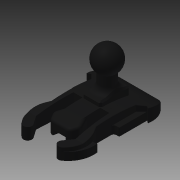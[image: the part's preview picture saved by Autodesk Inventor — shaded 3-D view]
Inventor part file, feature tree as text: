
AUTODESK INVENTOR PART (.ipt)
format: ipt  version: 2014 (Build 180170000, 170)  size: 611,840 bytes
history: native  units: in
note: dims shown in document units (in); Inventor stores cm internally (conversion verified against a paired STEP export)
features: sketch x4, other x3, extrude x3, chamfer x2, plane x1, revolve x1, fillet x1, imported_body x1
ambient origin geometry x8: Origin, YZ Plane, XZ Plane, XY Plane, X Axis, Y Axis, Z Axis, Center Point
bodies: Body1 (feature_tree)
feature tree (16):
  other  "Cut-Extrude3"
  other  "Quck Release - Mount - Standard (1)1"
  extrude  "Extrusion1"  [1 undecoded]
  plane  "Work Plane1"
  extrude  "Extrusion2"  Depth=0.3in
  extrude  "Extrusion3"  Depth=0.5in
  other  "Work Axis1"
  revolve  "Revolution1"  [1 undecoded]
  fillet  "Fillet1"  Radius=0.03in
  chamfer  "Chamfer1"  Distance=0.03in Angle=45.0deg
  chamfer  "Chamfer2"  [1 undecoded]
  imported_body  "Base1"
  sketch  "Sketch1"  dims[d0=1.0in d1=0.0in d2=-0.4in]
  sketch  "Sketch2"  dims[d3=0.3in d4=0.0in d5=0.3in]
  sketch  "Sketch3"  dims[d6=0.5in d7=0.0in d8=0.5in]
  sketch  "Sketch4"  dims[d9=90.0deg d10=0.125in d11=0.03in d12=0.125in d13=45.0deg d14=0.03in d15=0.125in d16=45.0deg]
note: 3 required parameter values undecoded (feature->parameter linkage not recoverable at this tier; creation-order binding heuristic only, values carry confidence <= 0.55)